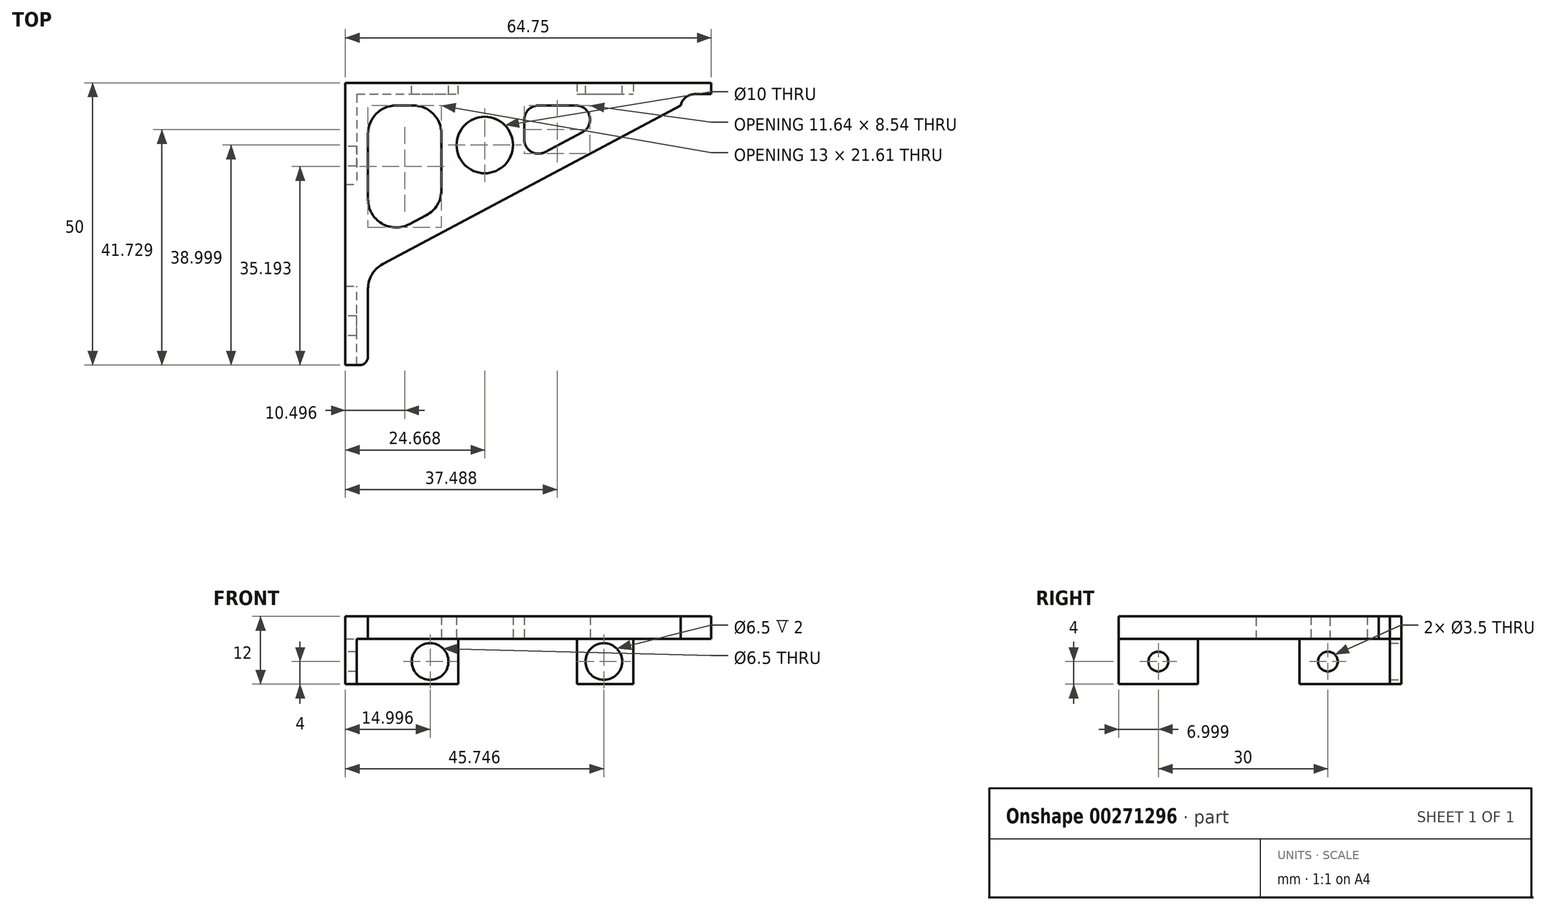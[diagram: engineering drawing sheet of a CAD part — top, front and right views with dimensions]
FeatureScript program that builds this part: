
annotation { "Feature Type Name" : "Feature", "Feature Type Description" : "" }
export const myFeature = defineFeature(function(context is Context, id is Id, definition is map)
    precondition{}
    {
        {
            var Q0;
            Q0=qCreatedBy(makeId("Top.planeOp"),FACE);
            var sketch = newSketch(context, id + "F0", { "sketchPlane" : qUnion([Q0])});
            skLineSegment(sketch, "E0.left", {"start": v(-24.04, 11.1) * mm, "end": v(-24.04, -13.83) * mm});
            skLineSegment(sketch, "E1", {"start": v(-28.04, 15.1) * mm, "end": v(-28.04, -34.9) * mm});
            skLineSegment(sketch, "E2", {"start": v(36.7, 15.1) * mm, "end": v(-28.04, 15.1) * mm});
            skLineSegment(sketch, "E3", {"start": v(-28.04, -34.9) * mm, "end": v(-24.04, -34.9) * mm});
            skLineSegment(sketch, "E4", {"start": v(-24.04, -34.9) * mm, "end": v(-24.04, -18.37) * mm});
            skLineSegment(sketch, "E5", {"start": v(-24.04, 11.1) * mm, "end": v(31.3, 11.1) * mm});
            skLineSegment(sketch, "E6", {"start": v(36.7, 15.1) * mm, "end": v(36.7, 13.1) * mm});
            skLineSegment(sketch, "E7", {"start": v(36.7, 13.1) * mm, "end": v(31.3, 13.1) * mm});
            skLineSegment(sketch, "E8", {"start": v(31.3, 13.1) * mm, "end": v(31.3, 11.1) * mm});
            skLineSegment(sketch, "E9", {"start": v(-24.04, -18.37) * mm, "end": v(31.3, 11.1) * mm});
            skLineSegment(sketch, "E10", {"start": v(-24.04, -13.83) * mm, "end": v(22.8, 11.1) * mm});
            skCircle(sketch, "E11", {"center": v(-3.37, 4.1) * mm, "radius": 5 * mm});
            skLineSegment(sketch, "E12", {"start": v(-11.04, 11.1) * mm, "end": v(-11.04, -6.91) * mm});
            skLineSegment(sketch, "E13", {"start": v(3.63, 11.1) * mm, "end": v(3.63, 0.9) * mm});
            skSolve(sketch);
        }
        {
            var Q0;
            {var subQ7=sQuery(id+"F0.wireOp",EDGE,"E0.left");Q0=makeQuery(id+"F0.imprint","IMPRINT",FACE,{"disambiguationData":[TD([[makeQuery(id+"F0.imprint","IMPRINT",EDGE,{"derivedFrom":subQ7}),-1.0]])]});}
            var Q1;
            Q1=makeQuery(id+"F0.imprint","IMPRINT",FACE,{"disambiguationData":[TD([[makeQuery(id+"F0.imprint","IMPRINT",EDGE,{"derivedFrom":sQuery(id+"F0.wireOp",EDGE,"E11")}),-1.0]])]});
            extrude(context, id + "F1", {"entities" : qUnion([Q0, Q1]), "depth" : 4 * mm});
        }
        {
            var Q0;
            Q0=qCreatedBy(makeId("Top.planeOp"),FACE);
            var sketch = newSketch(context, id + "F2", { "sketchPlane" : qUnion([Q0])});
            skLineSegment(sketch, "E14.bottom", {"start": v(-28.04, 15.1) * mm, "end": v(-26.04, 15.1) * mm});
            skLineSegment(sketch, "E14.top", {"start": v(-28.04, -2.9) * mm, "end": v(-26.04, -2.9) * mm});
            skLineSegment(sketch, "E14.left", {"start": v(-28.04, 15.1) * mm, "end": v(-28.04, -2.9) * mm});
            skLineSegment(sketch, "E14.right", {"start": v(-26.04, 15.1) * mm, "end": v(-26.04, -2.9) * mm});
            skLineSegment(sketch, "E15.bottom", {"start": v(-26.04, 13.1) * mm, "end": v(-8.04, 13.1) * mm});
            skLineSegment(sketch, "E15.top", {"start": v(-26.04, 15.1) * mm, "end": v(-8.04, 15.1) * mm});
            skLineSegment(sketch, "E15.left", {"start": v(-26.04, 13.1) * mm, "end": v(-26.04, 15.1) * mm});
            skLineSegment(sketch, "E15.right", {"start": v(-8.04, 13.1) * mm, "end": v(-8.04, 15.1) * mm});
            skLineSegment(sketch, "E16.bottom", {"start": v(-28.04, -34.9) * mm, "end": v(-26.04, -34.9) * mm});
            skLineSegment(sketch, "E16.top", {"start": v(-28.04, -20.9) * mm, "end": v(-26.04, -20.9) * mm});
            skLineSegment(sketch, "E16.left", {"start": v(-28.04, -34.9) * mm, "end": v(-28.04, -20.9) * mm});
            skLineSegment(sketch, "E16.right", {"start": v(-26.04, -34.9) * mm, "end": v(-26.04, -20.9) * mm});
            skLineSegment(sketch, "E17.bottom", {"start": v(12.96, 15.1) * mm, "end": v(22.96, 15.1) * mm});
            skLineSegment(sketch, "E17.top", {"start": v(12.96, 13.1) * mm, "end": v(22.96, 13.1) * mm});
            skLineSegment(sketch, "E17.left", {"start": v(12.96, 15.1) * mm, "end": v(12.96, 13.1) * mm});
            skLineSegment(sketch, "E17.right", {"start": v(22.96, 15.1) * mm, "end": v(22.96, 13.1) * mm});
            skSolve(sketch);
        }
        {
            var Q0;
            Q0=makeQuery(id+"F2.imprint","IMPRINT",FACE,{"disambiguationData":[TD([[makeQuery(id+"F2.imprint","IMPRINT",EDGE,{"derivedFrom":sQuery(id+"F2.wireOp",EDGE,"E17.bottom")}),-1.0]])]});
            var Q1;
            Q1=makeQuery(id+"F2.imprint","IMPRINT",FACE,{"disambiguationData":[TD([[makeQuery(id+"F2.imprint","IMPRINT",EDGE,{"derivedFrom":sQuery(id+"F2.wireOp",EDGE,"E15.bottom")}),1.0]])]});
            var Q2;
            Q2=makeQuery(id+"F2.imprint","IMPRINT",FACE,{"disambiguationData":[TD([[makeQuery(id+"F2.imprint","IMPRINT",EDGE,{"derivedFrom":sQuery(id+"F2.wireOp",EDGE,"E14.bottom")}),-1.0]])]});
            var Q3;
            Q3=makeQuery(id+"F2.imprint","IMPRINT",FACE,{"disambiguationData":[TD([[makeQuery(id+"F2.imprint","IMPRINT",EDGE,{"derivedFrom":sQuery(id+"F2.wireOp",EDGE,"E16.bottom")}),1.0]])]});
            extrude(context, id + "F3", {"entities" : qUnion([Q0, Q1, Q2, Q3]), "operationType" : NewBodyOperationType.ADD, "oppositeDirection" : true, "depth" : 8 * mm});
        }
        {
            var Q0;
            Q0=makeQuery(id+"F1.opExtrude","SWEPT_EDGE",EDGE,{"disambiguationData":[OSD([sQuery(id+"F0.wireOp",EDGE,"E4"),sQuery(id+"F0.wireOp",EDGE,"E9")])]});
            var Q1;
            Q1=makeQuery(id+"F1.opExtrude","SWEPT_EDGE",EDGE,{"disambiguationData":[OSD([sQuery(id+"F0.wireOp",EDGE,"E0.left"),sQuery(id+"F0.wireOp",EDGE,"E5")])]});
            var Q2;
            Q2=makeQuery(id+"F3.opExtrude","CAP_EDGE",EDGE,{"disambiguationData":[OSD([sQuery(id+"F2.wireOp",EDGE,"E15.right")])],"isStart":true});
            var Q3;
            Q3=makeQuery(id+"F3.opExtrude","CAP_EDGE",EDGE,{"disambiguationData":[OSD([sQuery(id+"F2.wireOp",EDGE,"E17.right")])],"isStart":true});
            var Q4;
            Q4=makeQuery(id+"F3.opExtrude","CAP_EDGE",EDGE,{"disambiguationData":[OSD([sQuery(id+"F2.wireOp",EDGE,"E14.top")])],"isStart":true});
            var Q5;
            Q5=makeQuery(id+"F3.opExtrude","CAP_EDGE",EDGE,{"disambiguationData":[OSD([sQuery(id+"F2.wireOp",EDGE,"E17.left")])],"isStart":true});
            var Q6;
            Q6=makeQuery(id+"F3.opExtrude","CAP_EDGE",EDGE,{"disambiguationData":[OSD([sQuery(id+"F2.wireOp",EDGE,"E16.top")])],"isStart":true});
            var Q7;
            Q7=makeQuery(id+"F1.opExtrude","SWEPT_EDGE",EDGE,{"disambiguationData":[OSD([sQuery(id+"F0.wireOp",EDGE,"E10"),sQuery(id+"F0.wireOp",EDGE,"E12")])]});
            var Q8;
            Q8=makeQuery(id+"F1.opExtrude","SWEPT_EDGE",EDGE,{"disambiguationData":[OSD([sQuery(id+"F0.wireOp",EDGE,"E0.left"),sQuery(id+"F0.wireOp",EDGE,"E10")])]});
            var Q9;
            Q9=makeQuery(id+"F1.opExtrude","SWEPT_EDGE",EDGE,{"disambiguationData":[OSD([sQuery(id+"F0.wireOp",EDGE,"E5"),sQuery(id+"F0.wireOp",EDGE,"E12")])]});
            fillet(context, id + "F4", {"entities" : qUnion([Q0, Q1, Q2, Q3, Q4, Q5, Q6, Q7, Q8, Q9]), "radius" : 5 * mm, "tangentPropagation" : true, "allowEdgeOverflow" : false});
        }
        {
            var Q0;
            Q0=makeQuery(id+"F1.opExtrude","SWEPT_EDGE",EDGE,{"disambiguationData":[OSD([sQuery(id+"F0.wireOp",EDGE,"E7"),sQuery(id+"F0.wireOp",EDGE,"E8")])]});
            var Q1;
            Q1=makeQuery(id+"F1.opExtrude","SWEPT_EDGE",EDGE,{"disambiguationData":[OSD([sQuery(id+"F0.wireOp",EDGE,"E5"),sQuery(id+"F0.wireOp",EDGE,"E10")])]});
            var Q2;
            Q2=makeQuery(id+"F1.opExtrude","SWEPT_EDGE",EDGE,{"disambiguationData":[OSD([sQuery(id+"F0.wireOp",EDGE,"E10"),sQuery(id+"F0.wireOp",EDGE,"E13")])]});
            var Q3;
            Q3=makeQuery(id+"F1.opExtrude","SWEPT_EDGE",EDGE,{"disambiguationData":[OSD([sQuery(id+"F0.wireOp",EDGE,"E5"),sQuery(id+"F0.wireOp",EDGE,"E13")])]});
            fillet(context, id + "F5", {"entities" : qUnion([Q0, Q1, Q2, Q3]), "radius" : 2.5 * mm, "tangentPropagation" : true, "allowEdgeOverflow" : false});
        }
        {
            var Q0;
            Q0=makeQuery(id+"F1.opExtrude","SWEPT_EDGE",EDGE,{"disambiguationData":[OSD([sQuery(id+"F0.wireOp",EDGE,"E3"),sQuery(id+"F0.wireOp",EDGE,"E4")])]});
            fillet(context, id + "F6", {"entities" : qUnion([Q0]), "radius" : 1.5 * mm, "tangentPropagation" : true, "allowEdgeOverflow" : false});
        }
        {
            var Q0;
            Q0=makeQuery(id+"F3.boolean.opBoolean","MERGE",FACE,{"derivedFrom":[makeQuery(id+"F1.opExtrude","SWEPT_FACE",FACE,{"disambiguationData":[OSD([sQuery(id+"F0.wireOp",EDGE,"E1")])]}),makeQuery(id+"F3.opExtrude","SWEPT_FACE",FACE,{"disambiguationData":[OSD([sQuery(id+"F2.wireOp",EDGE,"E14.left")])]}),makeQuery(id+"F3.opExtrude","SWEPT_FACE",FACE,{"disambiguationData":[OSD([sQuery(id+"F2.wireOp",EDGE,"E16.left")])]})]});
            var sketch = newSketch(context, id + "F7", { "sketchPlane" : qUnion([Q0])});
            skLineSegment(sketch, "E18.bottom", {"start": v(-15.1, -8) * mm, "end": v(2.9, -8) * mm});
            skLineSegment(sketch, "E18.top", {"start": v(-15.1, 0) * mm, "end": v(2.9, 0) * mm});
            skLineSegment(sketch, "E18.left", {"start": v(-15.1, -8) * mm, "end": v(-15.1, 0) * mm});
            skLineSegment(sketch, "E18.right", {"start": v(2.9, -8) * mm, "end": v(2.9, 0) * mm});
            skLineSegment(sketch, "E19.bottom", {"start": v(34.9, 0) * mm, "end": v(20.9, 0) * mm});
            skLineSegment(sketch, "E19.top", {"start": v(34.9, -8) * mm, "end": v(20.9, -8) * mm});
            skLineSegment(sketch, "E19.left", {"start": v(34.9, 0) * mm, "end": v(34.9, -8) * mm});
            skLineSegment(sketch, "E19.right", {"start": v(20.9, 0) * mm, "end": v(20.9, -8) * mm});
            skCircle(sketch, "E20", {"center": v(-2.1, -4) * mm, "radius": 1.75 * mm});
            skCircle(sketch, "E21", {"center": v(27.9, -4) * mm, "radius": 1.75 * mm});
            skSolve(sketch);
        }
        {
            var Q0;
            Q0=makeQuery(id+"F3.boolean.opBoolean","MERGE",FACE,{"derivedFrom":[makeQuery(id+"F1.opExtrude","SWEPT_FACE",FACE,{"disambiguationData":[OSD([sQuery(id+"F0.wireOp",EDGE,"E2")])]}),makeQuery(id+"F3.opExtrude","SWEPT_FACE",FACE,{"disambiguationData":[OSD([sQuery(id+"F2.wireOp",EDGE,"E14.bottom"),sQuery(id+"F2.wireOp",EDGE,"E15.top")])]}),makeQuery(id+"F3.opExtrude","SWEPT_FACE",FACE,{"disambiguationData":[OSD([sQuery(id+"F2.wireOp",EDGE,"E17.bottom")])]})]});
            var sketch = newSketch(context, id + "F8", { "sketchPlane" : qUnion([Q0])});
            skPoint(sketch, "E22.oppositeSnap0", {"position": v(28.04, -6) * mm});
            skLineSegment(sketch, "E22.bottom", {"start": v(8.04, 0) * mm, "end": v(28.04, 0) * mm});
            skLineSegment(sketch, "E22.top", {"start": v(8.04, -8) * mm, "end": v(28.04, -8) * mm});
            skLineSegment(sketch, "E22.left", {"start": v(8.04, 0) * mm, "end": v(8.04, -8) * mm});
            skLineSegment(sketch, "E22.right", {"start": v(28.04, 0) * mm, "end": v(28.04, -8) * mm});
            skCircle(sketch, "E23", {"center": v(-17.7, -4) * mm, "radius": 3.25 * mm});
            skCircle(sketch, "E24", {"center": v(13.04, -4) * mm, "radius": 3.25 * mm});
            skSolve(sketch);
        }
        {
            var Q0;
            Q0=makeQuery(id+"F8.imprint","IMPRINT",FACE,{"disambiguationData":[TD([[makeQuery(id+"F8.imprint","IMPRINT",EDGE,{"derivedFrom":sQuery(id+"F8.wireOp",EDGE,"E23")}),1.0]])]});
            var Q1;
            Q1=makeQuery(id+"F8.imprint","IMPRINT",FACE,{"disambiguationData":[TD([[makeQuery(id+"F8.imprint","IMPRINT",EDGE,{"derivedFrom":sQuery(id+"F8.wireOp",EDGE,"E24")}),1.0]])]});
            extrude(context, id + "F9", {"entities" : qUnion([Q0, Q1]), "operationType" : NewBodyOperationType.REMOVE, "oppositeDirection" : true, "depth" : 2 * mm});
        }
        {
            var Q0;
            Q0=makeQuery(id+"F7.imprint","IMPRINT",FACE,{"disambiguationData":[TD([[makeQuery(id+"F7.imprint","IMPRINT",EDGE,{"derivedFrom":sQuery(id+"F7.wireOp",EDGE,"E21")}),1.0]])]});
            var Q1;
            Q1=makeQuery(id+"F7.imprint","IMPRINT",FACE,{"disambiguationData":[TD([[makeQuery(id+"F7.imprint","IMPRINT",EDGE,{"derivedFrom":sQuery(id+"F7.wireOp",EDGE,"E20")}),1.0]])]});
            extrude(context, id + "F10", {"entities" : qUnion([Q0, Q1]), "operationType" : NewBodyOperationType.REMOVE, "oppositeDirection" : true, "depth" : 2 * mm});
        }
    });
